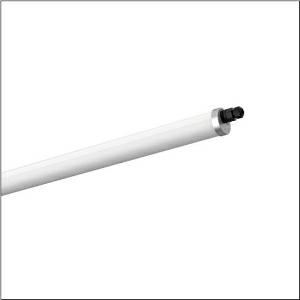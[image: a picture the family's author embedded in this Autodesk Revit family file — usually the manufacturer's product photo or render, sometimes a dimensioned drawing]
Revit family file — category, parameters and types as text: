
# Revit family: monsun_31_tube_51ft107n460a
name_source: partatom
category: Lighting Fixtures
units: mm (PartAtom-declared; Revit-internal decimal feet)

## family parameters
Cut with Voids When Loaded = No
Host = Face
Light Source = No
Part Type = Normal
Room Calculation Point = No
Round Connector Dimension = Use Diameter
Shared = No

## types (1)
- Monsun 31 Tube (1 x LED, 6500 lm, 40 W, 4000K)
    Apparent Load = 40 VA
    CIE Flux Codes = 42 71 90 91 100
    Color Rendering = 80
    Color Temperature = 4000K
    Default Elevation = 1800 mm
    Description = Monsun 31 Tube, tubular luminaire, primary optical cover: diffuser, of PMMA, light emission: direct distribution, primary light characteristic: symmetric, installation type: suspended mounting, surface-mounted, LED, rated luminous flux: 6.500lm, luminous efficacy: 160lm/W, light colour: 840, colour temperature: 4000K, control gear: ON/OFF, with with 1 terminal, 3-pole, max. 2.5mm², through-wiring: 3x 1.5mm², mains connection: 220..240V, AC, 50/60Hz, rated input power: 40W, housing, cylindrical, of PMMA, semi-transparent, matt white, with luminaire and ceiling fastening, V4A, mounting with brackets of stainless steel, length: 1.560mm, diameter: 75mm, end cap, of stainless steel (V4A), protection rating (complete): IP67/IP69K, insulation class (complete): insulation class I (protective earthing), certification: CE, UKCA, impact resistance: IK07, permissible operating ambient temperature: -20..+40°C, corresponds to IFS (International Featured Standards) requirements for safety and quality in the food industry, usage in unprotected outdoor areas possible with horizontal mounting, contact your sales advisor before using the luminaires in applications with unclear chemical exposure, large temperature fluctuations or condensation-forming humidity, packaging unit: 1 piece
    Height = 83 mm
    Lamp = 1 x LED
    Lamp Light Flux = 6500 lm
    Lamp Power = 40 W
    Lamp count = 1
    Length = 1560 mm
    Luminous efficacy = 163 lm/W
    Manufacturer = Siteco
    ModVariant = No
    Model = 51FT107N460A
    Mounting Place = Ceiling
    Mounting Type = Pendant
    Number of Poles = 1
    OnlyDefault = Yes
    Power Factor = 1
    Product Name = Monsun 31 Tube
    Product group = tubular luminaire
    ProductGroupID = 906
    Protection Class = Protection class I
    RLX_Detail_Level = 1
    RLX_Emergency_Light_Flux = 0 lm
    RLX_Emergency_Type = 0
    RLX_Emergency_Type_DB = No
    RlxData = <blob elided: 25285 chars, md5=ae99ab00>
    Socket = socket
    Standby Power = 0 W
    System Light Flux = 6500 lm
    System Power = 40 W
    Type Comments = Product without accessories
    Type Image = l_1228461.jpg
    URL = http://relux.com
    VarID = ---
    Voltage = 0 V
    Weight = 0.00 kg
    Width = 75 mm

## geometry (parser evidence)
native form markers: Blend x4, Sweep x13
no freeform markers — native parametric forms only
